# Revit family: Haworth_Maari_Stool_CounterHeight
name_source: partatom
category: Furniture
revit_build: Autodesk Revit 2018 (Build: 20170223_1515(x64)
units: mm (PartAtom-declared; Revit-internal decimal feet)

## family parameters
Always vertical = Yes
Cut with Voids When Loaded = No
OmniClass Number = 23.40.70.14.64.21
OmniClass Title = Systems Furniture
Room Calculation Point = No
Shared = No
Work Plane-Based = No

## types (6) — shared parameters
Actual Depth = 23"
Actual Width = 23"
Arm Cap Finish = Haworth _ Polymer _ Water TR-1W
Assembly Code = E2020200
Manufacturer = Haworth
Model = Haworth - Stool - Maari
Revision Number = 2
Size = Verify Final Dim. w/ Haworth
Sustainability Info = https://www.haworth.com
URL = www.haworth.com
URL - Product = https://www.haworth.com
Warranty = http://www.haworth.com

## per-type parameters (varying)
| type | Actual Height | Arms Control | Description | Four Legs | Low Back | Sled Base | Standard Back | With Arms | Wood Base |
| S7HC Sled Base - Standard Back - No Arms | 41 1/2" | No | Haworth Stool Maari Counter Height - Sled Base - Standard Back - No Arms | No | No | Yes | Yes | No | No |
| S7SC Four Legs - Standard Back - With Arms | 41 1/2" | Yes | Haworth Stool Maari Counter Height - Four Legs - Standard Back - With Arms | Yes | No | No | Yes | Yes | No |
| S7WC Wood Leg - Standard Back - No Arms | 41 1/2" | No | Haworth Stool Maari Counter Height - Wood Leg - Standard Back - No Arms | No | No | No | Yes | No | Yes |
| S8HC Sled Base - Low Back - No Arms | 31 1/4" | No | Haworth Stool Maari Counter Height - Sled Base - Low Back - No Arms | No | Yes | Yes | No | No | No |
| S7SC Four Legs - Standard Back - No Arms | 41 1/2" | No | Haworth Stool Maari Counter Height - Four Legs - Standard Back - No Arms | Yes | No | No | Yes | No | No |
| S8WC Wood Leg - Low Back - No Arms | 31 1/4" | No | Haworth Stool Maari Counter Height - Wood Leg - Standard Back - No Arms | No | Yes | No | No | No | Yes |

## geometry (parser evidence)
native form markers: Blend x4, Sweep x4
no freeform markers — native parametric forms only
